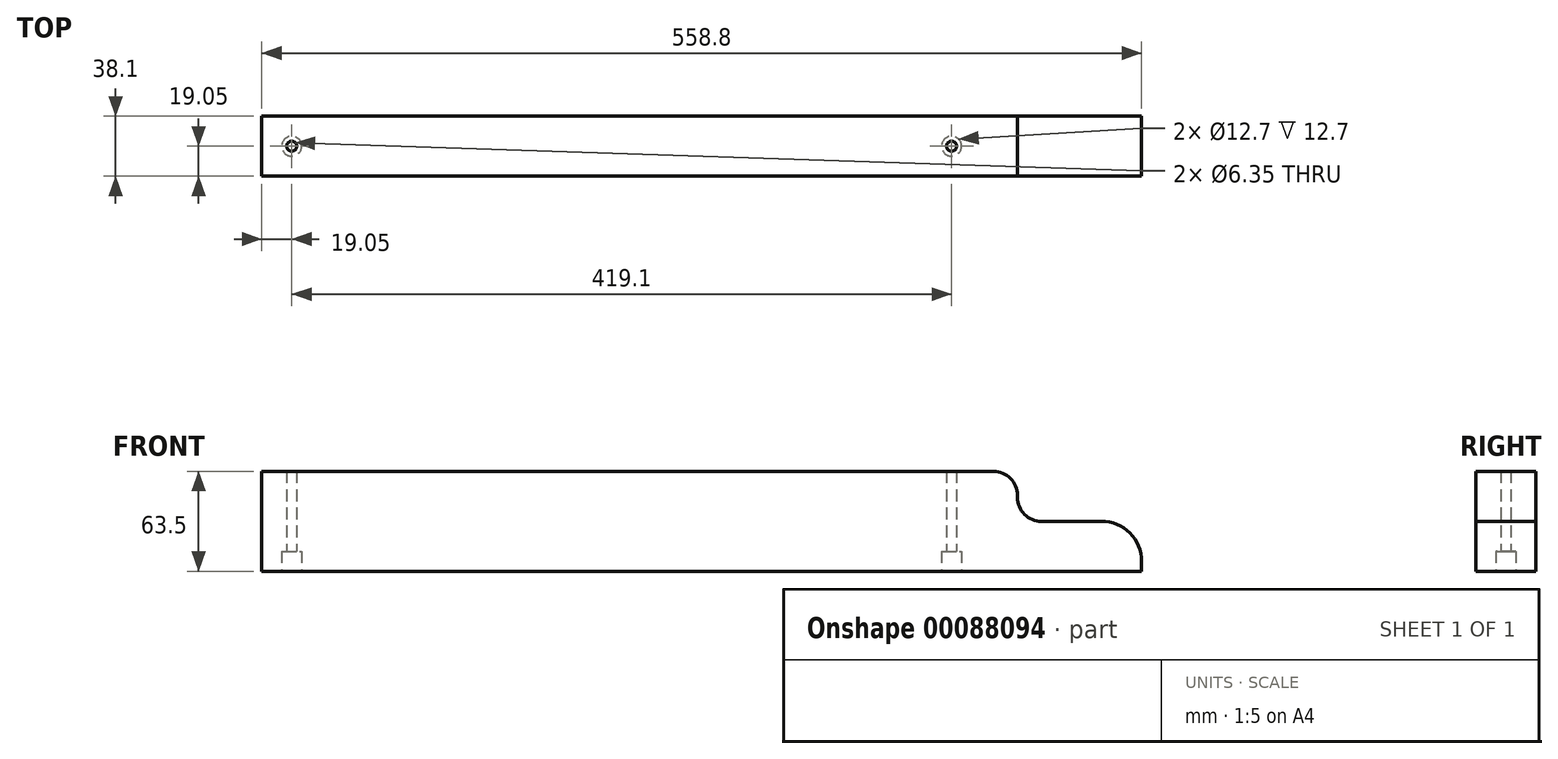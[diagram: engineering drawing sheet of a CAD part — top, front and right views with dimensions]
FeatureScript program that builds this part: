
annotation { "Feature Type Name" : "Feature", "Feature Type Description" : "" }
export const myFeature = defineFeature(function(context is Context, id is Id, definition is map)
    precondition{}
    {
        {
            var Q0;
            Q0=qCreatedBy(makeId("Right.planeOp"),FACE);
            var sketch = newSketch(context, id + "F0", { "sketchPlane" : qUnion([Q0])});
            skLineSegment(sketch, "E0.bottom", {"start": v(-19.05, 31.75) * mm, "end": v(19.05, 31.75) * mm});
            skLineSegment(sketch, "E0.top", {"start": v(-19.05, -31.75) * mm, "end": v(19.05, -31.75) * mm});
            skLineSegment(sketch, "E0.left", {"start": v(-19.05, 31.75) * mm, "end": v(-19.05, -31.75) * mm});
            skLineSegment(sketch, "E0.right", {"start": v(19.05, 31.75) * mm, "end": v(19.05, -31.75) * mm});
            skSolve(sketch);
        }
        {
            var Q0;
            Q0=makeQuery(id+"F0.imprint","IMPRINT",FACE,{"disambiguationData":[TD([[makeQuery(id+"F0.imprint","IMPRINT",EDGE,{"derivedFrom":sQuery(id+"F0.wireOp",EDGE,"E0.bottom")}),-1.0]])]});
            extrude(context, id + "F1", {"entities" : qUnion([Q0]), "endBound" : BoundingType.SYMMETRIC, "depth" : 558.8 * mm});
        }
        {
            var Q0;
            Q0=makeQuery(id+"F1.opExtrude","SWEPT_FACE",FACE,{"disambiguationData":[OSD([sQuery(id+"F0.wireOp",EDGE,"E0.left")])]});
            var sketch = newSketch(context, id + "F2", { "sketchPlane" : qUnion([Q0])});
            skLineSegment(sketch, "E1", {"start": v(152.4, 31.75) * mm, "end": v(152.4, -31.75) * mm, "construction": true});
            skLineSegment(sketch, "E2", {"start": v(279.4, 0) * mm, "end": v(152.4, 0) * mm, "construction": true});
            skLineSegment(sketch, "E3", {"start": v(279.4, -25.4) * mm, "end": v(249.2, -25.4) * mm, "construction": true});
            skLineSegment(sketch, "E4", {"start": v(254, 0) * mm, "end": v(254, -31.75) * mm, "construction": true});
            skArc(sketch, "E5", {"start": v(279.4, -25.4) * mm, "mid": v(271.96, -7.44) * mm, "end": v(254, 0) * mm});
            skLineSegment(sketch, "E6", {"start": v(215.9, 31.75) * mm, "end": v(215.9, -31.75) * mm, "construction": true});
            skLineSegment(sketch, "E7", {"start": v(200.66, 31.75) * mm, "end": v(200.66, -31.75) * mm, "construction": true});
            skLineSegment(sketch, "E8", {"start": v(185.42, 31.75) * mm, "end": v(185.42, -31.75) * mm, "construction": true});
            skLineSegment(sketch, "E9", {"start": v(279.4, 15.24) * mm, "end": v(205.34, 15.24) * mm, "construction": true});
            skLineSegment(sketch, "E10", {"start": v(279.4, 16.51) * mm, "end": v(217.49, 16.51) * mm, "construction": true});
            skArc(sketch, "E11", {"start": v(215.9, 0) * mm, "mid": v(205.12, 4.46) * mm, "end": v(200.66, 15.24) * mm});
            skArc(sketch, "E12", {"start": v(200.66, 16.51) * mm, "mid": v(196.19, 27.28) * mm, "end": v(185.42, 31.75) * mm});
            skLineSegment(sketch, "E13", {"start": v(200.66, 16.51) * mm, "end": v(200.66, 15.24) * mm});
            skLineSegment(sketch, "E14", {"start": v(185.42, 31.75) * mm, "end": v(279.4, 31.75) * mm});
            skLineSegment(sketch, "E15", {"start": v(279.4, 31.75) * mm, "end": v(279.4, -25.4) * mm});
            skLineSegment(sketch, "E16", {"start": v(254, 0) * mm, "end": v(215.9, 0) * mm});
            skSolve(sketch);
        }
        {
            var Q0;
            Q0=makeQuery(id+"F2.imprint","IMPRINT",FACE,{"disambiguationData":[TD([[makeQuery(id+"F2.imprint","IMPRINT",EDGE,{"derivedFrom":sQuery(id+"F2.wireOp",EDGE,"E5")}),-1.0]])]});
            extrude(context, id + "F3", {"entities" : qUnion([Q0]), "operationType" : NewBodyOperationType.REMOVE, "endBound" : BoundingType.THROUGH_ALL, "oppositeDirection" : true, "depth" : 25.4 * mm});
        }
        {
            var Q0;
            Q0=makeQuery(id+"F1.opExtrude","SWEPT_FACE",FACE,{"disambiguationData":[OSD([sQuery(id+"F0.wireOp",EDGE,"E0.top")])]});
            var sketch = newSketch(context, id + "F4", { "sketchPlane" : qUnion([Q0])});
            skLineSegment(sketch, "E17", {"start": v(-279.4, 0) * mm, "end": v(279.4, 0) * mm, "construction": true});
            skLineSegment(sketch, "E18", {"start": v(-260.35, 19.05) * mm, "end": v(-260.35, -19.05) * mm, "construction": true});
            skLineSegment(sketch, "E19", {"start": v(158.75, 19.05) * mm, "end": v(158.75, -19.05) * mm, "construction": true});
            skCircle(sketch, "E20", {"center": v(-260.35, 0) * mm, "radius": 6.35 * mm});
            skCircle(sketch, "E21", {"center": v(158.75, 0) * mm, "radius": 6.35 * mm});
            skSolve(sketch);
        }
        {
            var Q0;
            Q0=makeQuery(id+"F4.imprint","IMPRINT",FACE,{"disambiguationData":[TD([[makeQuery(id+"F4.imprint","IMPRINT",EDGE,{"derivedFrom":sQuery(id+"F4.wireOp",EDGE,"E20")}),1.0]])]});
            var Q1;
            Q1=makeQuery(id+"F4.imprint","IMPRINT",FACE,{"disambiguationData":[TD([[makeQuery(id+"F4.imprint","IMPRINT",EDGE,{"derivedFrom":sQuery(id+"F4.wireOp",EDGE,"E21")}),1.0]])]});
            extrude(context, id + "F5", {"entities" : qUnion([Q0, Q1]), "operationType" : NewBodyOperationType.REMOVE, "oppositeDirection" : true, "depth" : 12.7 * mm});
        }
        {
            var Q0;
            Q0=makeQuery(id+"F5.boolean.opBoolean","COPY",FACE,{"derivedFrom":makeQuery(id+"F5.opExtrude","CAP_FACE",FACE,{"disambiguationData":[OSD([sQuery(id+"F4.wireOp",EDGE,"E20")])],"isStart":false})});
            var sketch = newSketch(context, id + "F6", { "sketchPlane" : qUnion([Q0])});
            skCircle(sketch, "E22.0", {"center": v(-260.35, 0) * mm, "radius": 6.35 * mm});
            skCircle(sketch, "E23.0", {"center": v(158.75, 0) * mm, "radius": 6.35 * mm});
            skCircle(sketch, "E24", {"center": v(-260.35, 0) * mm, "radius": 3.18 * mm});
            skCircle(sketch, "E25", {"center": v(158.75, 0) * mm, "radius": 3.18 * mm});
            skSolve(sketch);
        }
        {
            var Q0;
            Q0=makeQuery(id+"F6.imprint","IMPRINT",FACE,{"disambiguationData":[TD([[makeQuery(id+"F6.imprint","IMPRINT",EDGE,{"derivedFrom":sQuery(id+"F6.wireOp",EDGE,"E24")}),1.0]])]});
            var Q1;
            Q1=makeQuery(id+"F6.imprint","IMPRINT",FACE,{"disambiguationData":[TD([[makeQuery(id+"F6.imprint","IMPRINT",EDGE,{"derivedFrom":sQuery(id+"F6.wireOp",EDGE,"E25")}),1.0]])]});
            extrude(context, id + "F7", {"entities" : qUnion([Q0, Q1]), "operationType" : NewBodyOperationType.REMOVE, "endBound" : BoundingType.THROUGH_ALL, "oppositeDirection" : true, "depth" : 25.4 * mm});
        }
    });
